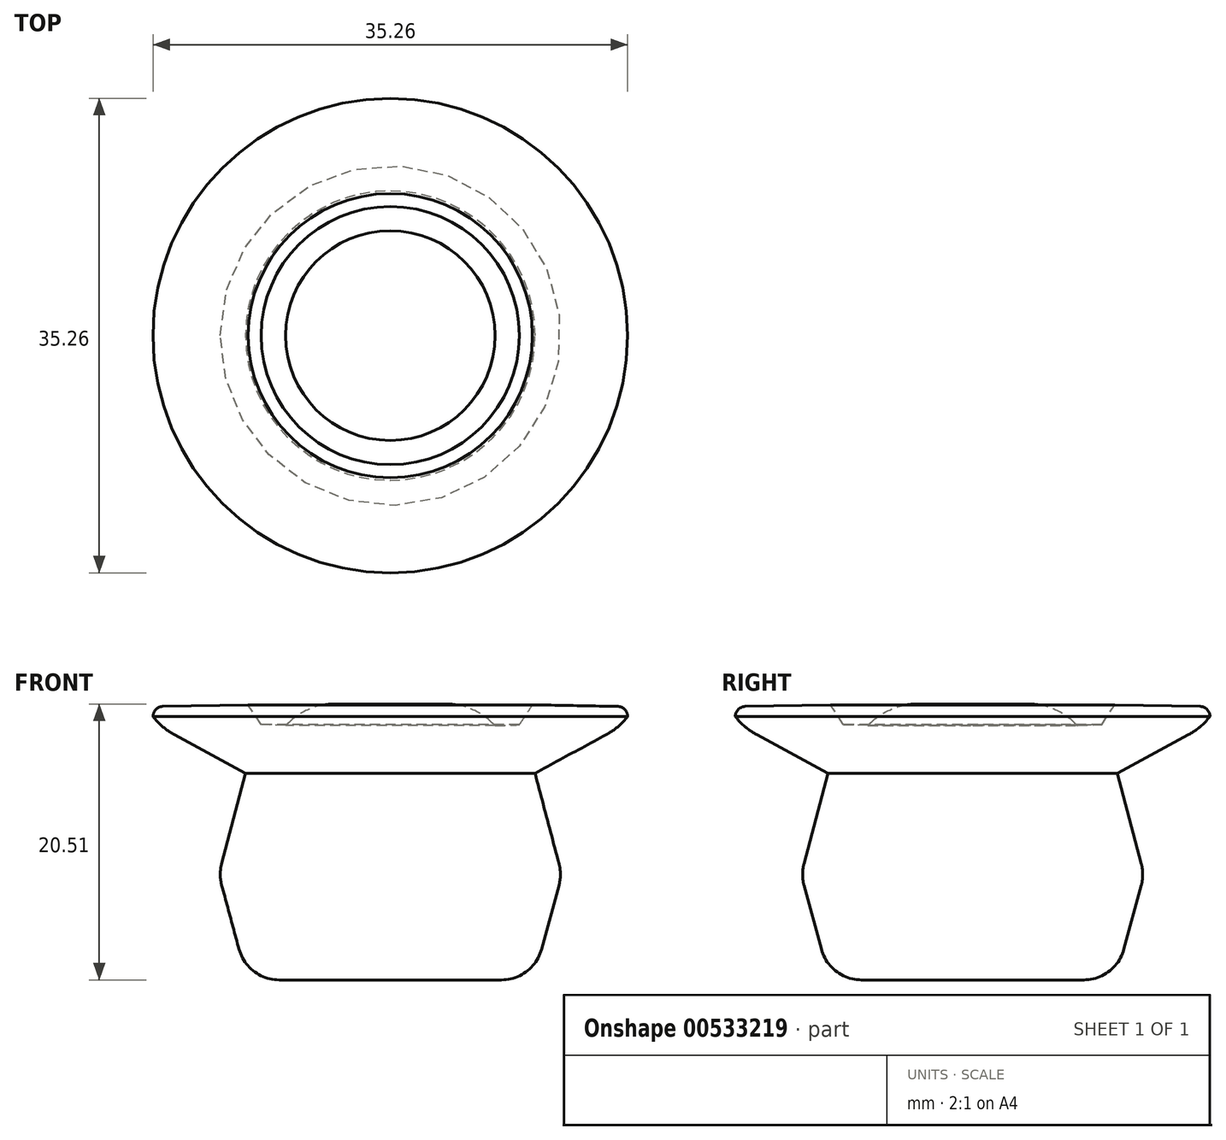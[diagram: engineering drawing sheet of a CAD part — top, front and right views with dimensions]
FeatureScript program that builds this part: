
annotation { "Feature Type Name" : "Feature", "Feature Type Description" : "" }
export const myFeature = defineFeature(function(context is Context, id is Id, definition is map)
    precondition{}
    {
        {
            var Q0;
            Q0=qCreatedBy(makeId("Front.planeOp"),FACE);
            var sketch = newSketch(context, id + "F0", { "sketchPlane" : qUnion([Q0])});
            skLineSegment(sketch, "E0", {"start": v(0, 0) * mm, "end": v(-10.62, 0) * mm});
            skLineSegment(sketch, "E1", {"start": v(-10.62, 0) * mm, "end": v(-12.74, 7.84) * mm});
            skLineSegment(sketch, "E2", {"start": v(-12.74, 7.84) * mm, "end": v(-10.75, 15.36) * mm});
            skLineSegment(sketch, "E3", {"start": v(-10.75, 15.36) * mm, "end": v(-17.63, 19.1) * mm});
            skLineSegment(sketch, "E4", {"start": v(-17.63, 19.1) * mm, "end": v(-17.63, 20.32) * mm});
            skLineSegment(sketch, "E5", {"start": v(-17.63, 20.32) * mm, "end": v(-10.56, 20.44) * mm});
            skLineSegment(sketch, "E6", {"start": v(-10.56, 20.44) * mm, "end": v(-9.6, 18.96) * mm});
            skLineSegment(sketch, "E7", {"start": v(-9.6, 18.96) * mm, "end": v(-7.79, 18.9) * mm});
            skLineSegment(sketch, "E8", {"start": v(-7.79, 18.9) * mm, "end": v(-6.12, 20.5) * mm});
            skLineSegment(sketch, "E9", {"start": v(-6.12, 20.5) * mm, "end": v(0, 20.5) * mm});
            skLineSegment(sketch, "E10", {"start": v(0, 20.5) * mm, "end": v(0, 0) * mm});
            skSolve(sketch);
        }
        {
            var Q0;
            Q0=makeQuery(id+"F0.imprint","IMPRINT",FACE,{"disambiguationData":[TD([[makeQuery(id+"F0.imprint","IMPRINT",EDGE,{"derivedFrom":sQuery(id+"F0.wireOp",EDGE,"E0")}),-1.0]])]});
            var Q1;
            Q1=sQuery(id+"F0.wireOp",EDGE,"E10");
            revolve(context, id + "F1", {"entities" : qUnion([Q0]), "axis" : qUnion([Q1]), "revolveType" : RevolveType.FULL});
        }
        {
            var Q0;
            Q0=makeQuery(id+"F1.opRevolve","SWEPT_EDGE",EDGE,{"disambiguationData":[OSD([sQuery(id+"F0.wireOp",EDGE,"E8"),sQuery(id+"F0.wireOp",EDGE,"E9")])]});
            fillet(context, id + "F2", {"entities" : qUnion([Q0]), "radius" : 5 * mm, "tangentPropagation" : true, "allowEdgeOverflow" : false});
        }
        {
            var Q0;
            Q0=makeQuery(id+"F1.opRevolve","SWEPT_EDGE",EDGE,{"disambiguationData":[OSD([sQuery(id+"F0.wireOp",EDGE,"E4"),sQuery(id+"F0.wireOp",EDGE,"E5")])]});
            fillet(context, id + "F3", {"entities" : qUnion([Q0]), "radius" : 0.75 * mm, "tangentPropagation" : true, "allowEdgeOverflow" : false});
        }
        {
            var Q0;
            Q0=makeQuery(id+"F1.opRevolve","SWEPT_EDGE",EDGE,{"disambiguationData":[OSD([sQuery(id+"F0.wireOp",EDGE,"E3"),sQuery(id+"F0.wireOp",EDGE,"E4")])]});
            fillet(context, id + "F4", {"entities" : qUnion([Q0]), "radius" : 5 * mm, "tangentPropagation" : true, "allowEdgeOverflow" : false});
        }
        {
            var Q0;
            Q0=makeQuery(id+"F1.opRevolve","SWEPT_FACE",FACE,{"disambiguationData":[OSD([sQuery(id+"F0.wireOp",EDGE,"E1")])]});
            fillet(context, id + "F5", {"entities" : qUnion([Q0]), "radius" : 3.09 * mm, "tangentPropagation" : true, "allowEdgeOverflow" : false});
        }
    });
